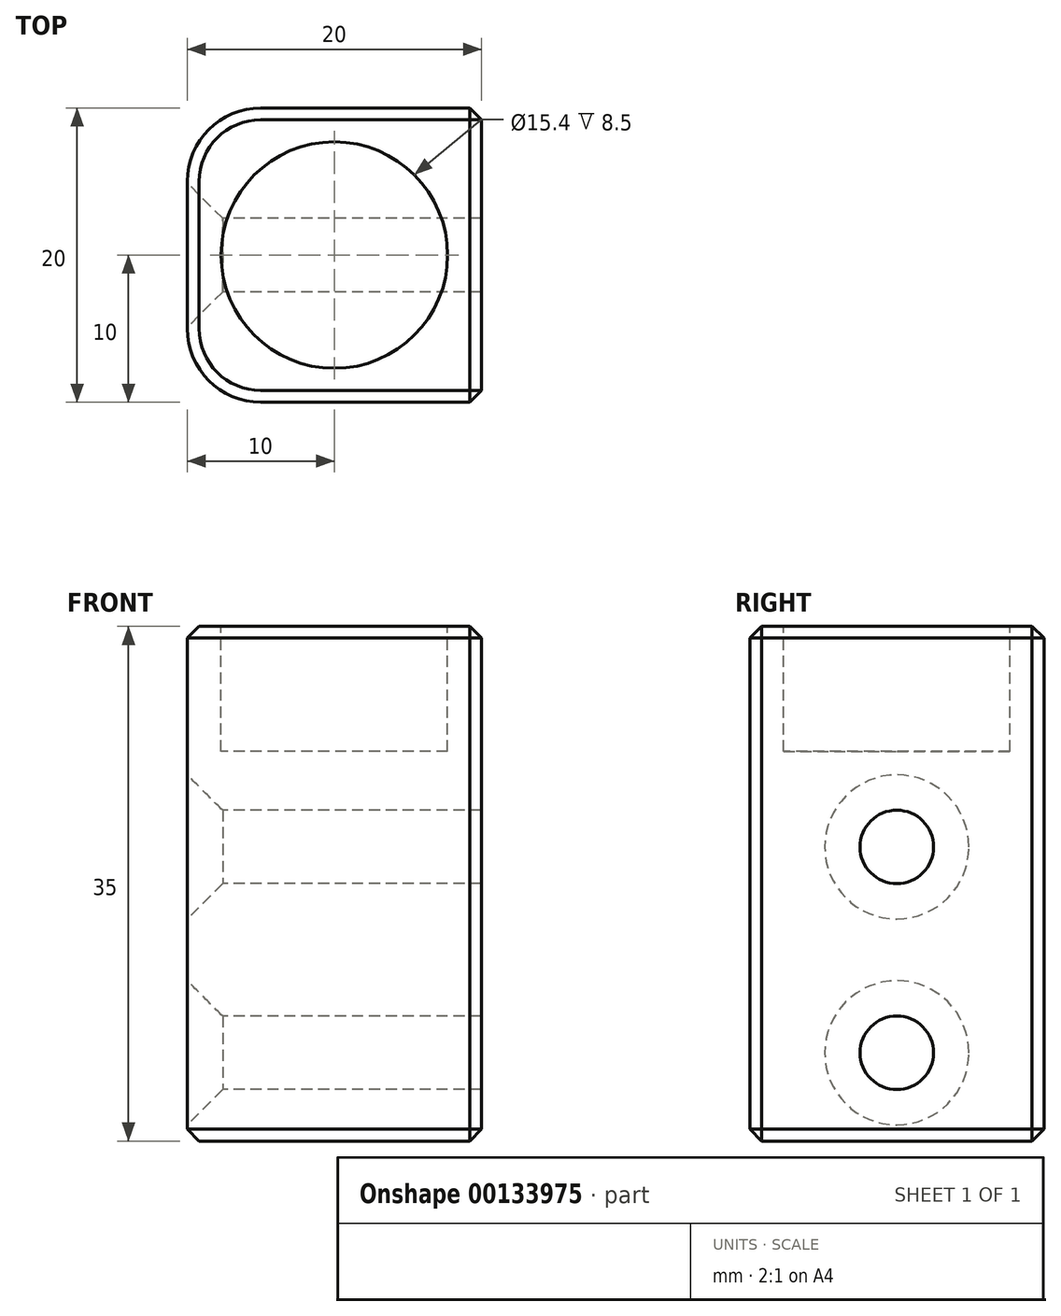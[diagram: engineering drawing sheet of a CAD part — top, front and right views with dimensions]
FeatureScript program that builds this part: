
annotation { "Feature Type Name" : "Feature", "Feature Type Description" : "" }
export const myFeature = defineFeature(function(context is Context, id is Id, definition is map)
    precondition{}
    {
        {
            var Q0;
            Q0=qCreatedBy(makeId("Top.planeOp"),FACE);
            var sketch = newSketch(context, id + "F0", { "sketchPlane" : qUnion([Q0])});
            skLineSegment(sketch, "E0.bottom", {"start": v(10, -10) * mm, "end": v(-10, -10) * mm});
            skLineSegment(sketch, "E0.top", {"start": v(10, 10) * mm, "end": v(-10, 10) * mm});
            skLineSegment(sketch, "E0.left", {"start": v(10, -10) * mm, "end": v(10, 10) * mm});
            skLineSegment(sketch, "E0.right", {"start": v(-10, -10) * mm, "end": v(-10, 10) * mm});
            skPoint(sketch, "E0.middle", {"position": v(0, 0) * mm});
            skSolve(sketch);
        }
        {
            var Q0;
            Q0 = qSketchRegion(id + "F0", true);
            extrude(context, id + "F1", {"entities" : qUnion([Q0]), "depth" : 35 * mm, "offsetDistance" : 25 * mm});
        }
        {
            var Q0;
            Q0=makeQuery(id+"F1.opExtrude","CAP_FACE",FACE,{"disambiguationData":[OSD([sQuery(id+"F0.wireOp",EDGE,"E0.bottom"),sQuery(id+"F0.wireOp",EDGE,"E0.top"),sQuery(id+"F0.wireOp",EDGE,"E0.left"),sQuery(id+"F0.wireOp",EDGE,"E0.right")])],"isStart":false});
            var sketch = newSketch(context, id + "F2", { "sketchPlane" : qUnion([Q0])});
            skCircle(sketch, "E1", {"center": v(0, 0) * mm, "radius": 7.7 * mm});
            skSolve(sketch);
        }
        {
            var Q0;
            Q0=makeQuery(id+"F2.imprint","IMPRINT",FACE,{"disambiguationData":[TD([[makeQuery(id+"F2.imprint","IMPRINT",EDGE,{"derivedFrom":sQuery(id+"F2.wireOp",EDGE,"E1")}),1.0]])]});
            extrude(context, id + "F3", {"entities" : qUnion([Q0]), "operationType" : NewBodyOperationType.REMOVE, "oppositeDirection" : true, "depth" : 8.5 * mm, "offsetDistance" : 25 * mm});
        }
        {
            var Q0;
            Q0=makeQuery(id+"F1.opExtrude","SWEPT_FACE",FACE,{"disambiguationData":[OSD([sQuery(id+"F0.wireOp",EDGE,"E0.right")])]});
            var sketch = newSketch(context, id + "F4", { "sketchPlane" : qUnion([Q0])});
            skPoint(sketch, "E2", {"position": v(0, 6) * mm});
            skPoint(sketch, "E3", {"position": v(0, 20) * mm});
            skSolve(sketch);
        }
        {
            var Q0;
            Q0=sQuery(id+"F4.wireOp",VERTEX,"E2");
            var Q1;
            Q1=sQuery(id+"F4.wireOp",VERTEX,"E3");
            var Q2;
            Q2=makeQuery(id+"F1.opExtrude","SWEPT_BODY",BODY,{"disambiguationData":[OSD([sQuery(id+"F0.wireOp",EDGE,"E0.bottom"),sQuery(id+"F0.wireOp",EDGE,"E0.top"),sQuery(id+"F0.wireOp",EDGE,"E0.left"),sQuery(id+"F0.wireOp",EDGE,"E0.right")])]});
            hole(context, id + "F5", {"style" : HoleStyle.C_SINK, "endStyle" : HoleEndStyle.THROUGH, "holeDiameter" : 5 * mm, "cSinkDiameter" : 9.8 * mm, "cSinkAngle" : 90 * degree, "majorDiameter" : 5 * mm, "isTappedThrough" : true, "tappedDepth" : 12 * mm, "tapClearance" : 3, "startFromSketch" : true, "locations" : qUnion([Q0, Q1]), "scope" : qUnion([Q2])});
        }
        {
            var Q0;
            Q0=makeQuery(id+"F1.opExtrude","SWEPT_EDGE",EDGE,{"disambiguationData":[OSD([sQuery(id+"F0.wireOp",EDGE,"E0.bottom"),sQuery(id+"F0.wireOp",EDGE,"E0.right")])]});
            var Q1;
            Q1=makeQuery(id+"F1.opExtrude","SWEPT_EDGE",EDGE,{"disambiguationData":[OSD([sQuery(id+"F0.wireOp",EDGE,"E0.top"),sQuery(id+"F0.wireOp",EDGE,"E0.right")])]});
            fillet(context, id + "F6", {"entities" : qUnion([Q0, Q1]), "radius" : 5 * mm, "tangentPropagation" : true, "allowEdgeOverflow" : false});
        }
        {
            var Q0;
            Q0=makeQuery(id+"F3.boolean.opBoolean","COPY",EDGE,{"derivedFrom":makeQuery(id+"F3.opExtrude","CAP_EDGE",EDGE,{"disambiguationData":[OSD([sQuery(id+"F2.wireOp",EDGE,"E1")])],"isStart":true})});
            var Q1;
            Q1=makeQuery(id+"F1.opExtrude","SWEPT_EDGE",EDGE,{"disambiguationData":[OSD([sQuery(id+"F0.wireOp",EDGE,"E0.bottom"),sQuery(id+"F0.wireOp",EDGE,"E0.left")])]});
            var Q2;
            Q2=makeQuery(id+"F1.opExtrude","SWEPT_EDGE",EDGE,{"disambiguationData":[OSD([sQuery(id+"F0.wireOp",EDGE,"E0.top"),sQuery(id+"F0.wireOp",EDGE,"E0.left")])]});
            var Q3;
            Q3=makeQuery(id+"F1.opExtrude","CAP_EDGE",EDGE,{"disambiguationData":[OSD([sQuery(id+"F0.wireOp",EDGE,"E0.top")])],"isStart":false});
            var Q4;
            Q4=makeQuery(id+"F1.opExtrude","CAP_EDGE",EDGE,{"disambiguationData":[OSD([sQuery(id+"F0.wireOp",EDGE,"E0.right")])],"isStart":false});
            var Q5;
            Q5=makeQuery(id+"F1.opExtrude","CAP_EDGE",EDGE,{"disambiguationData":[OSD([sQuery(id+"F0.wireOp",EDGE,"E0.left")])],"isStart":false});
            var Q6;
            Q6=makeQuery(id+"F1.opExtrude","CAP_EDGE",EDGE,{"disambiguationData":[OSD([sQuery(id+"F0.wireOp",EDGE,"E0.right")])],"isStart":true});
            var Q7;
            Q7=makeQuery(id+"F1.opExtrude","CAP_EDGE",EDGE,{"disambiguationData":[OSD([sQuery(id+"F0.wireOp",EDGE,"E0.top")])],"isStart":true});
            var Q8;
            Q8=makeQuery(id+"F1.opExtrude","CAP_EDGE",EDGE,{"disambiguationData":[OSD([sQuery(id+"F0.wireOp",EDGE,"E0.left")])],"isStart":true});
            var Q9;
            Q9=makeQuery(id+"F1.opExtrude","CAP_EDGE",EDGE,{"disambiguationData":[OSD([sQuery(id+"F0.wireOp",EDGE,"E0.bottom")])],"isStart":true});
            var Q10;
            Q10=makeQuery(id+"F1.opExtrude","CAP_EDGE",EDGE,{"disambiguationData":[OSD([sQuery(id+"F0.wireOp",EDGE,"E0.bottom")])],"isStart":false});
            var Q11;
            Q11=makeQuery(id+"F5.hole-1.boolean.opBoolean","INTERSECT",EDGE,{"derivedFrom":[makeQuery(id+"F1.opExtrude","SWEPT_FACE",FACE,{"disambiguationData":[OSD([sQuery(id+"F0.wireOp",EDGE,"E0.left")])]}),makeQuery(id+"F5.hole-1.opRevolve","SWEPT_FACE",FACE,{"disambiguationData":[OSD([sQuery(id+"F5.hole-1.sketch.wireOp",EDGE,"core_line_2")])]})]});
            var Q12;
            Q12=makeQuery(id+"F5.hole-0.boolean.opBoolean","INTERSECT",EDGE,{"derivedFrom":[makeQuery(id+"F1.opExtrude","SWEPT_FACE",FACE,{"disambiguationData":[OSD([sQuery(id+"F0.wireOp",EDGE,"E0.left")])]}),makeQuery(id+"F5.hole-0.opRevolve","SWEPT_FACE",FACE,{"disambiguationData":[OSD([sQuery(id+"F5.hole-0.sketch.wireOp",EDGE,"core_line_2")])]})]});
            chamfer(context, id + "F7", {"entities" : qUnion([Q0, Q1, Q2, Q3, Q4, Q5, Q6, Q7, Q8, Q9, Q10, Q11, Q12]), "width" : 0.8 * mm, "tangentPropagation" : true});
        }
    });
